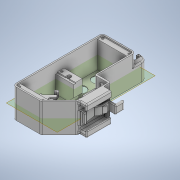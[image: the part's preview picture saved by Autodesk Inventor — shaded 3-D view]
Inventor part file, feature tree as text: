
AUTODESK INVENTOR PART (.ipt)
format: ipt  version: 2020.3 (Build 243373000, 373)  size: 1,413,632 bytes
history: native  units: mm
features: fillet x20, extrude x12, sketch x12, projected_geometry x4, plane x1, mirror x1, other x1
ambient origin geometry x8: Origin, YZ Plane, XZ Plane, XY Plane, X Axis, Y Axis, Z Axis, Center Point
bodies: Volumenkörper1 (feature_tree)
feature tree (51):
  extrude  "Extrusion1"  [1 undecoded]
  plane  "Arbeitsebene1"
  extrude  "Extrusion2"  Depth=1.0mm
  extrude  "Extrusion3"  Depth=3.0mm
  extrude  "Extrusion4"  Depth=2.0mm
  extrude  "Extrusion5"  Depth=12.0mm
  extrude  "Extrusion6"  Depth=3.0mm
  mirror  "Spiegeln1"
  fillet  "Rundung2"  Radius=2.2mm
  fillet  "Rundung3"  Radius=4.7mm
  fillet  "Rundung4"  Radius=13.0mm
  fillet  "Rundung5"  Radius=10.0mm
  fillet  "Rundung8"  Radius=4.0mm
  fillet  "Rundung9"  Radius=4.0mm
  fillet  "Rundung10"  Radius=3.0mm
  fillet  "Rundung11"  Radius=3.0mm
  sketch  "Skizze8"  dims[d11=30.0mm d12=4.5mm d13=2.2mm d14=4.7mm d15=13.0mm d16=10.0mm d17=4.0mm d18=4.0mm d19=3.0mm d20=3.0mm]
  extrude  "Extrusion8"  Depth=1.0mm
  extrude  "Extrusion9"  Depth=19.0mm TaperAngle=0.0deg
  extrude  "Extrusion10"  Depth=13.0mm
  extrude  "Extrusion11"  Depth=10.0mm
  fillet  "Rundung12"  Radius=10.0mm
  fillet  "Rundung13"  Radius=13.0mm
  extrude  "Extrusion12"  Depth=10.0mm TaperAngle=0.0deg
  fillet  "Rundung14"  Radius=10.0mm
  extrude  "Extrusion13"  Depth=1.0mm
  fillet  "Rundung15"  Radius=4.5mm
  fillet  "Rundung16"  Radius=3.0mm
  fillet  "Rundung17"  Radius=37.0mm
  fillet  "Rundung18"  Radius=2.0mm
  fillet  "Rundung19"  Radius=1.0mm
  fillet  "Rundung20"  Radius=2.0mm
  fillet  "Rundung21"  Radius=2.0mm
  fillet  "Rundung22"  [1 undecoded]
  fillet  "Rundung23"  [1 undecoded]
  sketch  "Skizze1"  dims[d0=0.0mm d1=0.0mm d2=-22.0mm]
  sketch  "Skizze2"  dims[d3=1.0mm d4=5.0mm]
  sketch  "Skizze3"  dims[d5=2.0mm d6=3.0mm]
  sketch  "Skizze4"  dims[d7=2.0mm d8=4.0mm]
  sketch  "Skizze5"  dims[d9=17.0mm d10=12.0mm]
  sketch  "Skizze9"  dims[d21=1.0mm d22=13.0mm]
  sketch  "Skizze10"  dims[d23=2.2mm d24=19.0mm d25=0.0mm]
  projected_geometry  "Projizierte Kontur1"
  projected_geometry  "Projizierte Kontur2"
  sketch  "Skizze11"  dims[d26=12.0mm d27=13.0mm]
  sketch  "Skizze12"  dims[d28=6.5mm d29=6.0mm d30=10.0mm d31=0.0mm d32=13.0mm]
  sketch  "Skizze13"  dims[d33=6.5mm d34=10.0mm d35=0.0mm d38=10.0mm d39=0.0mm]
  projected_geometry  "Projizierte Kontur3"
  projected_geometry  "Projizierte Kontur4"
  sketch  "Skizze14"  dims[d40=15.95mm d41=12.7mm d42=4.5mm d43=3.0mm d44=37.0mm d45=0.0mm d52=2.0mm d53=1.0mm d54=2.0mm d55=2.0mm d58=0.0mm d59=0.0mm d60=6.5mm d61=13.0mm d62=9.0mm d63=4.5mm d64=2.0mm d65=1.0mm d66=2.0mm d67=1.0mm d68=15.0mm d69=2.0mm d70=1.6mm d71=2.4mm d74=0.0mm d75=4.0mm d76=12.0mm d77=25.0mm d78=25.0mm d79=7.0mm d80=11.0mm d81=16.2mm d82=2.4mm d83=1.6mm d84=2.0mm d85=3.0mm d86=15.5mm d87=10.0mm d88=0.0mm d89=2.0mm d90=0.0mm d92=2.0mm d93=16.0mm d94=3.0mm d95=3.0mm d96=3.1mm d97=0.0mm d98=1.0mm d99=1.0mm d100=10.0mm d101=0.0mm d102=2.0mm d103=0.5mm d104=1.5mm d105=26.0mm d106=0.8mm d107=0.8mm d108=10.0mm d109=0.0mm d110=10.0mm d111=1.0mm d112=0.0mm d113=1.0mm d114=1.0mm d115=1.0mm d116=1.0mm d117=1.0mm d118=2.0mm d119=1.0mm d120=1.0mm d121=1.0mm]
  other  "Körper1"
note: 3 required parameter values undecoded (feature->parameter linkage not recoverable at this tier; creation-order binding heuristic only, values carry confidence <= 0.55)
